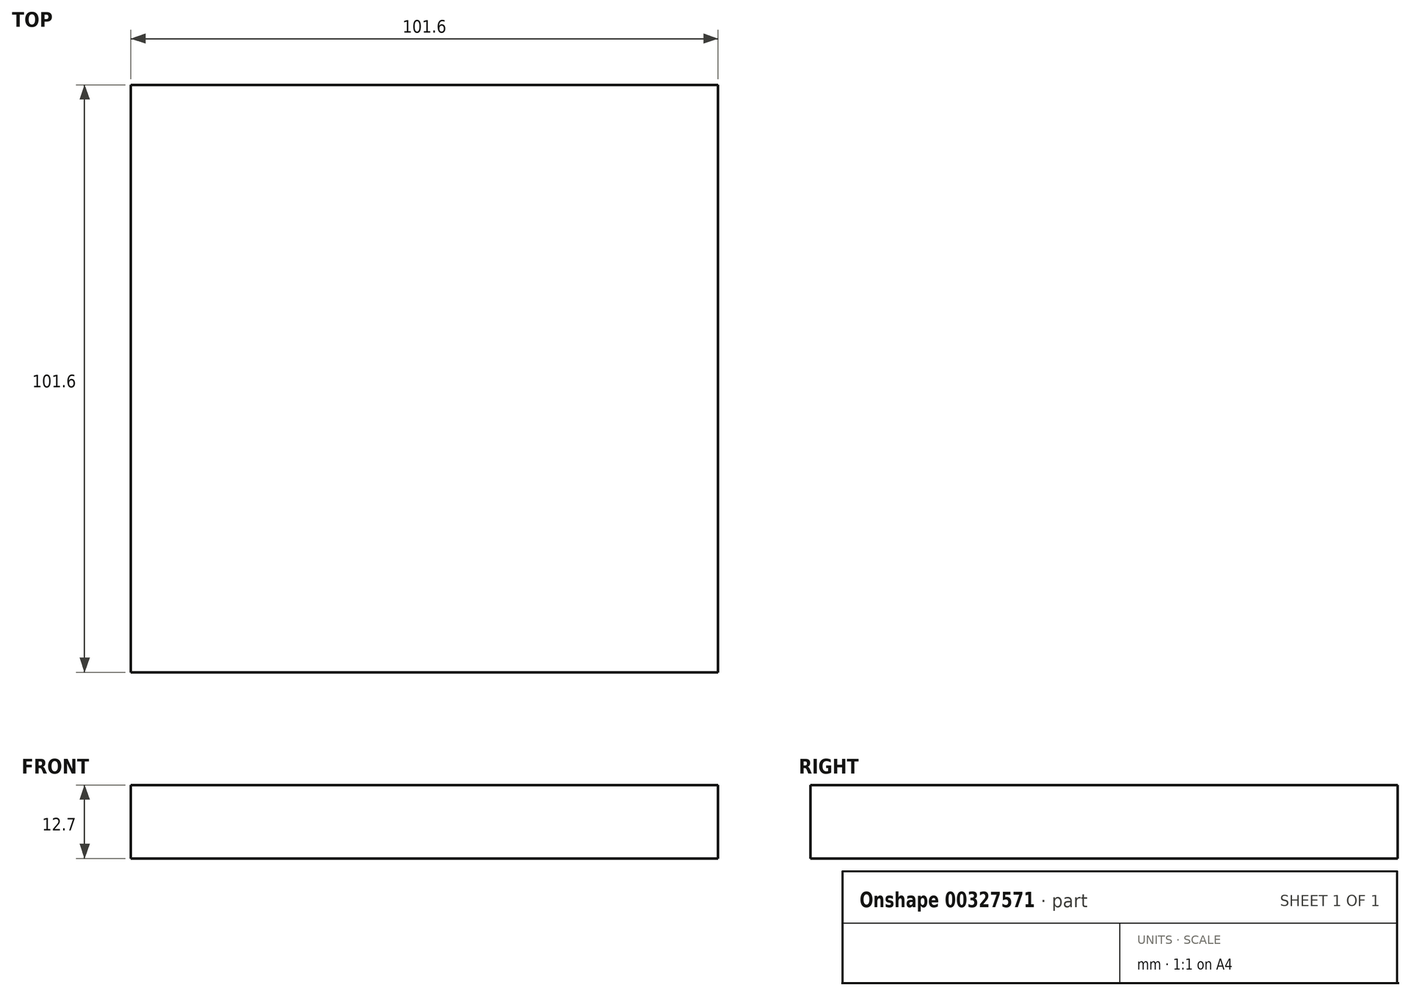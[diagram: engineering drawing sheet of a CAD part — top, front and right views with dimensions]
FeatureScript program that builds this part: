
annotation { "Feature Type Name" : "Feature", "Feature Type Description" : "" }
export const myFeature = defineFeature(function(context is Context, id is Id, definition is map)
    precondition{}
    {
        {
            var Q0;
            Q0=qCreatedBy(makeId("Top.planeOp"),FACE);
            var sketch = newSketch(context, id + "F0", { "sketchPlane" : qUnion([Q0])});
            skLineSegment(sketch, "E0.bottom", {"start": v(-43.8, 55.28) * mm, "end": v(57.8, 55.28) * mm});
            skLineSegment(sketch, "E0.top", {"start": v(-43.8, -46.32) * mm, "end": v(57.8, -46.32) * mm});
            skLineSegment(sketch, "E0.left", {"start": v(-43.8, 55.28) * mm, "end": v(-43.8, -46.32) * mm});
            skLineSegment(sketch, "E0.right", {"start": v(57.8, 55.28) * mm, "end": v(57.8, -46.32) * mm});
            skSolve(sketch);
        }
        {
            var Q0;
            Q0 = qSketchRegion(id + "F0", true);
            extrude(context, id + "F1", {"entities" : qUnion([Q0]), "depth" : 12.7 * mm});
        }
    });
